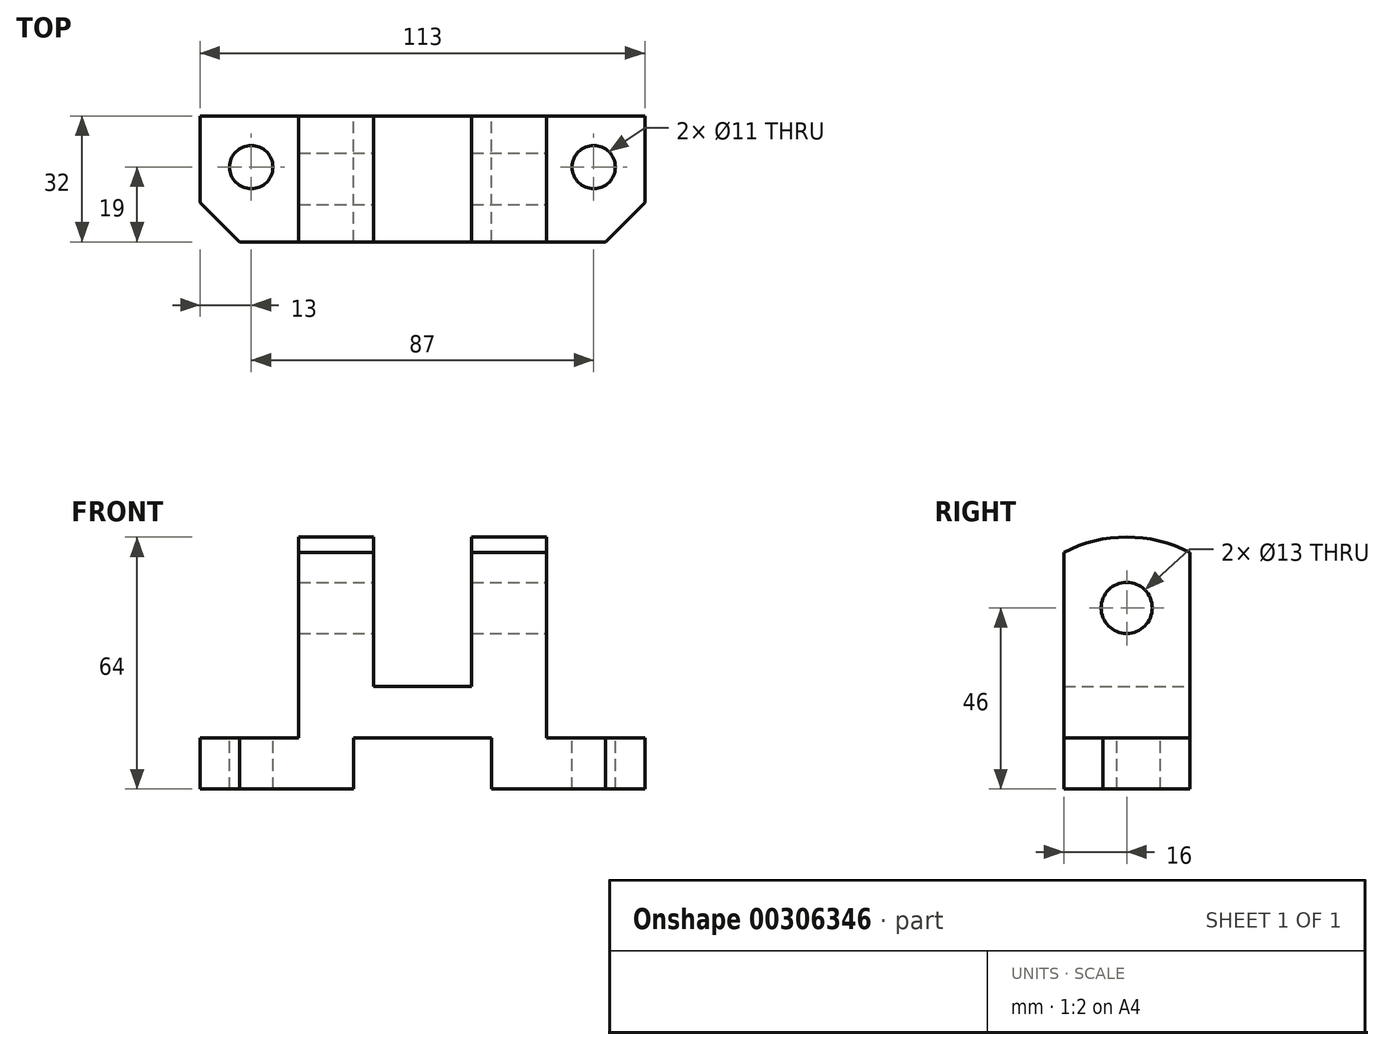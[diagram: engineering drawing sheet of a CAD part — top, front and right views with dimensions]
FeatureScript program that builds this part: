
annotation { "Feature Type Name" : "Feature", "Feature Type Description" : "" }
export const myFeature = defineFeature(function(context is Context, id is Id, definition is map)
    precondition{}
    {
        {
            var Q0;
            Q0=qCreatedBy(makeId("Front.planeOp"),FACE);
            var sketch = newSketch(context, id + "F0", { "sketchPlane" : qUnion([Q0])});
            skLineSegment(sketch, "E0", {"start": v(0, 0) * mm, "end": v(0, 13) * mm});
            skLineSegment(sketch, "E1", {"start": v(0, 13) * mm, "end": v(35, 13) * mm});
            skLineSegment(sketch, "E2", {"start": v(35, 13) * mm, "end": v(35, 0) * mm});
            skLineSegment(sketch, "E3", {"start": v(35, 0) * mm, "end": v(74, 0) * mm});
            skLineSegment(sketch, "E4", {"start": v(74, 0) * mm, "end": v(74, 13) * mm});
            skLineSegment(sketch, "E5", {"start": v(5, 64) * mm, "end": v(-14, 64) * mm});
            skLineSegment(sketch, "E6", {"start": v(-14, 64) * mm, "end": v(-14, 13) * mm});
            skLineSegment(sketch, "E7", {"start": v(-14, 13) * mm, "end": v(-39, 13) * mm});
            skLineSegment(sketch, "E8", {"start": v(-39, 13) * mm, "end": v(-39, 0) * mm});
            skLineSegment(sketch, "E9", {"start": v(-39, 0) * mm, "end": v(0, 0) * mm});
            skLineSegment(sketch, "E10", {"start": v(49, 64) * mm, "end": v(49, 13) * mm});
            skLineSegment(sketch, "E11", {"start": v(49, 13) * mm, "end": v(74, 13) * mm});
            skLineSegment(sketch, "E12", {"start": v(49, 64) * mm, "end": v(30, 64) * mm});
            skLineSegment(sketch, "E13", {"start": v(30, 64) * mm, "end": v(30, 26) * mm});
            skLineSegment(sketch, "E14", {"start": v(30, 26) * mm, "end": v(5, 26) * mm});
            skLineSegment(sketch, "E15", {"start": v(5, 26) * mm, "end": v(5, 64) * mm});
            skSolve(sketch);
        }
        {
            var Q0;
            Q0 = qSketchRegion(id + "F0", true);
            extrude(context, id + "F1", {"entities" : qUnion([Q0]), "depth" : 32 * mm});
        }
        {
            var Q0;
            Q0=makeQuery(id+"F1.opExtrude","SWEPT_FACE",FACE,{"disambiguationData":[OSD([sQuery(id+"F0.wireOp",EDGE,"E11")])]});
            var sketch = newSketch(context, id + "F2", { "sketchPlane" : qUnion([Q0])});
            skLineSegment(sketch, "E16", {"start": v(64, -32) * mm, "end": v(74, -22) * mm});
            skLineSegment(sketch, "E17", {"start": v(74, -22) * mm, "end": v(74, -32) * mm});
            skLineSegment(sketch, "E18", {"start": v(74, -32) * mm, "end": v(64, -32) * mm});
            skLineSegment(sketch, "E19", {"start": v(-29, -32) * mm, "end": v(-39, -22) * mm});
            skLineSegment(sketch, "E20", {"start": v(-39, -22) * mm, "end": v(-39, -32) * mm});
            skLineSegment(sketch, "E21", {"start": v(-39, -32) * mm, "end": v(-29, -32) * mm});
            skSolve(sketch);
        }
        {
            var Q0;
            Q0 = qSketchRegion(id + "F2", true);
            extrude(context, id + "F3", {"entities" : qUnion([Q0]), "operationType" : NewBodyOperationType.REMOVE, "endBound" : BoundingType.THROUGH_ALL, "oppositeDirection" : true, "depth" : 25 * mm});
        }
        {
            var Q0;
            Q0=makeQuery(id+"F1.opExtrude","SWEPT_FACE",FACE,{"disambiguationData":[OSD([sQuery(id+"F0.wireOp",EDGE,"E11")])]});
            var sketch = newSketch(context, id + "F4", { "sketchPlane" : qUnion([Q0])});
            skCircle(sketch, "E22", {"center": v(61, -13) * mm, "radius": 5.5 * mm});
            skCircle(sketch, "E23", {"center": v(-26, -13) * mm, "radius": 5.5 * mm});
            skSolve(sketch);
        }
        {
            var Q0;
            Q0=makeQuery(id+"F4.imprint","IMPRINT",FACE,{"disambiguationData":[TD([[makeQuery(id+"F4.imprint","IMPRINT",EDGE,{"derivedFrom":sQuery(id+"F4.wireOp",EDGE,"E23")}),1.0]])]});
            var Q1;
            Q1=makeQuery(id+"F4.imprint","IMPRINT",FACE,{"disambiguationData":[TD([[makeQuery(id+"F4.imprint","IMPRINT",EDGE,{"derivedFrom":sQuery(id+"F4.wireOp",EDGE,"E22")}),1.0]])]});
            extrude(context, id + "F5", {"entities" : qUnion([Q0, Q1]), "operationType" : NewBodyOperationType.REMOVE, "endBound" : BoundingType.THROUGH_ALL, "oppositeDirection" : true, "depth" : 25 * mm});
        }
        {
            var Q0;
            Q0=makeQuery(id+"F1.opExtrude","SWEPT_FACE",FACE,{"disambiguationData":[OSD([sQuery(id+"F0.wireOp",EDGE,"E10")])]});
            var sketch = newSketch(context, id + "F6", { "sketchPlane" : qUnion([Q0])});
            skCircle(sketch, "E24", {"center": v(-16, 46) * mm, "radius": 6.5 * mm});
            skSolve(sketch);
        }
        {
            var Q0;
            Q0 = qSketchRegion(id + "F6", true);
            extrude(context, id + "F7", {"entities" : qUnion([Q0]), "operationType" : NewBodyOperationType.REMOVE, "endBound" : BoundingType.THROUGH_ALL, "oppositeDirection" : true, "depth" : 25 * mm});
        }
        {
            var Q0;
            Q0=makeQuery(id+"F1.opExtrude","SWEPT_FACE",FACE,{"disambiguationData":[OSD([sQuery(id+"F0.wireOp",EDGE,"E10")])]});
            var sketch = newSketch(context, id + "F8", { "sketchPlane" : qUnion([Q0])});
            skArc(sketch, "E25", {"start": v(0, 60.13) * mm, "mid": v(-16, 64) * mm, "end": v(-32, 60.13) * mm});
            skLineSegment(sketch, "E26", {"start": v(-32, 60.13) * mm, "end": v(-32, 64) * mm});
            skLineSegment(sketch, "E27", {"start": v(0, 64) * mm, "end": v(0, 60.13) * mm});
            skLineSegment(sketch, "E28", {"start": v(-32, 64) * mm, "end": v(-16, 64) * mm});
            skLineSegment(sketch, "E29", {"start": v(-16, 64) * mm, "end": v(0, 64) * mm});
            skSolve(sketch);
        }
        {
            var Q0;
            Q0 = qSketchRegion(id + "F8", true);
            extrude(context, id + "F9", {"entities" : qUnion([Q0]), "operationType" : NewBodyOperationType.REMOVE, "endBound" : BoundingType.THROUGH_ALL, "oppositeDirection" : true, "depth" : 25 * mm});
        }
        {
            var Q0;
            Q0 = qSketchRegion(id + "F8", true);
            extrude(context, id + "F10", {"entities" : qUnion([Q0]), "operationType" : NewBodyOperationType.REMOVE, "endBound" : BoundingType.THROUGH_ALL, "oppositeDirection" : true, "depth" : 25 * mm});
        }
    });
